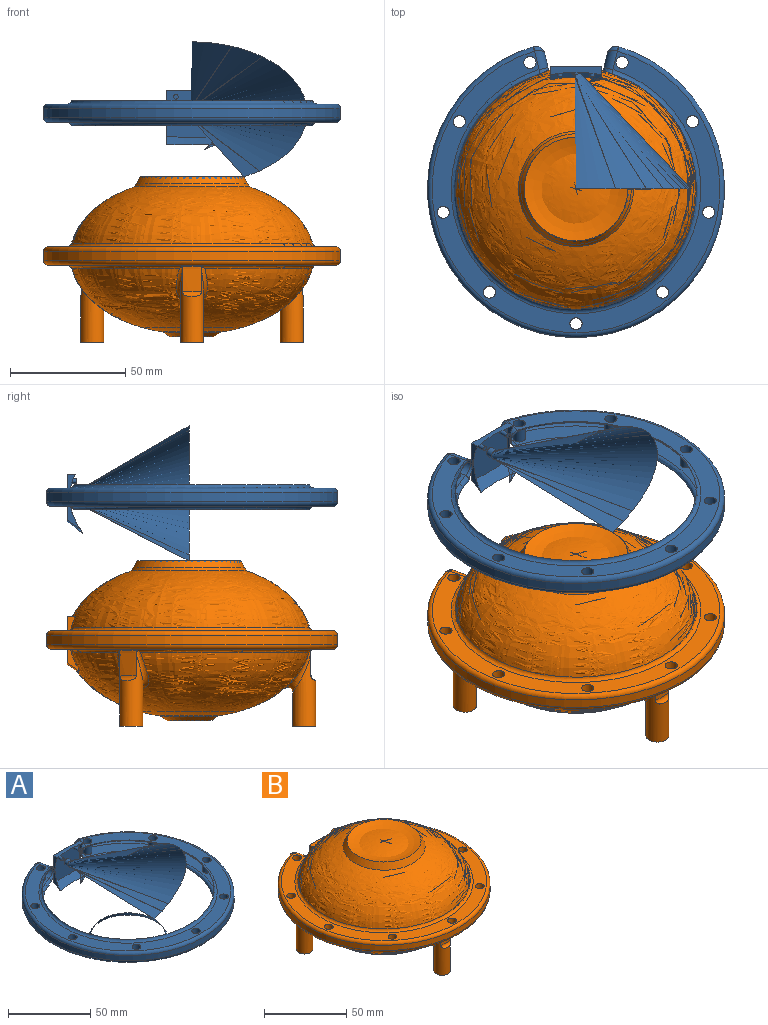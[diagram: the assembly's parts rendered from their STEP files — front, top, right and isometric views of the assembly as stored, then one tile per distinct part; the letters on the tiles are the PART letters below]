
ASSEMBLY  parts=2 mates=1
PART A: 52 faces, bbox 265.7x262.7x193.8 mm
  f0: plane 0.87x0.17mm, normal (0,0,-1), area 0.1mm2, adj f1,f50,f51
  f1: plane 22x20.66mm, normal (0,1,0), area 430mm2, adj f0,f2,f4,f5,f45,f46,f48,f50
  f2: cylinder r=2mm len=4mm, axis (0,-1,0), area 38.2mm2, adj f1,f3
  f3: revolved ~4x4mm, area 12.6mm2, adj f2
  f4: plane 0.87x0.17mm, normal (0,0,-1), area 0.1mm2, adj f1,f45,f50
  f5: plane 22x3.51mm, normal (0,0,1), area 59.5mm2, adj f1,f6,f45,f51
  f6: revolved ~105.61x105.6mm, area -70091.5mm2, adj f5,f7,f8,f37,f38,f39,f40,f41
  f7: plane 127.13x126.3mm, normal (0.97,-0.22,0), area 0.1mm2, adj f6,f8,f42
  f8: bspline ~6.62x5.74mm, area 9.9mm2, adj f6,f7,f9,f37
  f9: cylinder r=4mm len=8.95mm, axis (-0.22,-0.97,0), area 45.6mm2, adj f8,f10,f35,f36
  f10: cylinder r=4mm len=8.95mm, axis (0.22,0.97,0), area 45.6mm2, adj f9,f11,f34,f42
  f11: plane 125x122.37mm, normal (0,0,1), area 2542.7mm2, adj f10,f12,f22,f23,f24,f25,f26,f27
  f12: torus R=62.5mm, axis (0,0,1), area 1141.4mm2, adj f11,f13,f22,f24
  f13: cylinder r=64.5mm len=129mm, axis (0,0,1), area 1469.8mm2, adj f12,f14,f16,f21
  f14: cylinder r=4mm len=5.05mm, axis (0,0,1), area 17.1mm2, adj f13,f15,f22,f34,f35
  f15: torus R=2mm, axis (0,0,-1), area 0.7mm2, adj f14,f21,f35,f36
  f16: cylinder r=4mm len=5.05mm, axis (0,0,1), area 17.1mm2, adj f13,f17,f18,f20,f24
  f17: bspline ~5.54x4mm, area 8.7mm2, adj f16,f23,f24
  f18: bspline ~5.54x4mm, area 8.7mm2, adj f16,f19,f20
  f19: cylinder r=4mm len=8.95mm, axis (-0.22,0.97,0), area 45.6mm2, adj f18,f23,f36,f38
  f20: torus R=2mm, axis (0,0,-1), area 0.7mm2, adj f16,f18,f21,f36
  f21: torus R=62.5mm, axis (0,0,-1), area 1141.4mm2, adj f13,f15,f20,f36
  f22: torus R=2mm, axis (0,0,1), area 0.7mm2, adj f11,f12,f14,f34
  f23: cylinder r=4mm len=8.95mm, axis (0.22,-0.97,0), area 45.6mm2, adj f11,f17,f19,f40
  f24: torus R=2mm, axis (0,0,1), area 0.7mm2, adj f11,f12,f16,f17
  f25: cylinder r=2.65mm len=8mm, axis (0,0,1), area 133.2mm2, adj f11,f36
  f26: cylinder r=2.65mm len=8mm, axis (0,0,1), area 133.2mm2, adj f11,f36
  f27: cylinder r=2.65mm len=8mm, axis (0,0,1), area 133.2mm2, adj f11,f36
  f28: cylinder r=2.65mm len=8mm, axis (0,0,1), area 133.2mm2, adj f11,f36
  f29: cylinder r=2.65mm len=8mm, axis (0,0,1), area 133.2mm2, adj f11,f36
  f30: cylinder r=2.65mm len=8mm, axis (0,0,1), area 133.2mm2, adj f11,f36
  f31: cylinder r=2.65mm len=8mm, axis (0,0,1), area 133.2mm2, adj f11,f36
  f32: cylinder r=2.65mm len=8mm, axis (0,0,1), area 133.2mm2, adj f11,f36
  f33: cylinder r=2.65mm len=8mm, axis (0,0,1), area 133.2mm2, adj f11,f36
  f34: bspline ~5.54x4mm, area 8.7mm2, adj f10,f14,f22
  f35: bspline ~5.54x4mm, area 8.7mm2, adj f9,f14,f15
  f36: plane 125x122.37mm, normal (0,0,-1), area 2542.7mm2, adj f9,f15,f19,f20,f21,f25,f26,f27
  f37: torus R=54.25mm, axis (0,0,-1), area 798.1mm2, adj f6,f8,f36,f38
  f38: bspline ~6.62x5.74mm, area 9.9mm2, adj f6,f19,f37,f39
  f39: plane 127.13x126.3mm, normal (-0.97,-0.22,0), area 0.1mm2, adj f6,f38,f40
  f40: bspline ~6.62x5.74mm, area 9.9mm2, adj f6,f23,f39,f41
  f41: torus R=54.25mm, axis (0,0,-1), area 798.1mm2, adj f6,f11,f40,f42
  f42: bspline ~6.62x5.74mm, area 9.9mm2, adj f6,f7,f10,f41
  f43: cone r=22.5mm half-angle=29.3deg, axis (0,0,-1), area 447.5mm2, adj f6,f44
  f44: revolved ~22.5x22.5mm, area 0mm2, adj f43
  f45: plane 136.1x118.09mm, normal (-1,0,0), area 44.5mm2, adj f1,f4,f5,f6,f50
  f46: cylinder r=1mm len=4mm, axis (0,1,0), area 25.1mm2, adj f1,f47
  f47: plane 2x2mm, normal (0,1,0), area 3.1mm2, adj f46
  f48: cylinder r=1mm len=4mm, axis (0,1,0), area 25.1mm2, adj f1,f49
  f49: plane 2x2mm, normal (0,1,0), area 3.1mm2, adj f48
  f50: cone r=53.96mm half-angle=55.7deg, axis (0,0,1), area 128.5mm2, adj f0,f1,f4,f6,f45,f51
  f51: plane 129.26x111.26mm, normal (1,0,0), area 44.5mm2, adj f0,f1,f5,f6,f50
PART B: 84 faces, bbox 265.7x262.7x197.8 mm
  f0: revolved ~105.85x105.81mm, area -61415.2mm2, adj f4,f5,f6,f16,f17,f19,f21,f41
  f1: cylinder r=53mm len=11mm, axis (0,0,1), area 90.7mm2, adj f6,f35,f40,f55
  f2: cylinder r=53mm len=11mm, axis (0,0,1), area 90.7mm2, adj f5,f31,f39,f55
  f3: cylinder r=53mm len=11mm, axis (0,0,1), area 90.7mm2, adj f4,f26,f30,f55
  f4: bspline ~19.96x13.54mm, area 132mm2, adj f0,f3,f26,f55
  f5: bspline ~19.96x13.43mm, area 132mm2, adj f0,f2,f31,f55
  f6: bspline ~19.96x13.43mm, area 132mm2, adj f0,f1,f35,f55
  f7: revolved ~19x19mm, area 95.4mm2, adj f10,f44
  f8: revolved ~28x28mm, area 126.5mm2, adj f42,f43
  f9: plane 0.87x0.17mm, normal (0,0,-1), area 0.1mm2, adj f17,f20,f21
  f10: plane 15.5x15.5mm, normal (0,0,-1), area 45.6mm2, adj f7,f14
  f11: revolved ~99.99x99.97mm, area 11093.7mm2, adj f12,f15,f45
  f12: cylinder r=7.75mm len=15.5mm, axis (0,0,-1), area 98.1mm2, adj f11,f13
  f13: plane 15.5x15.5mm, normal (0,0,1), area 45.6mm2, adj f12,f14
  f14: cylinder r=6.75mm len=13.5mm, axis (0,0,-1), area 42.4mm2, adj f10,f13
  f15: cylinder r=2mm len=4mm, axis (0,-1,0), area 38.8mm2, adj f11,f20
  f16: plane 134.18x115.69mm, normal (0,0,1), area 59.5mm2, adj f0,f17,f19,f20
  f17: plane 129.32x111.32mm, normal (1,0,0), area 44.5mm2, adj f0,f9,f16,f20,f21
  f18: plane 0.87x0.17mm, normal (0,0,-1), area 0.1mm2, adj f19,f20,f21
  f19: plane 135.84x117.84mm, normal (-1,0,0), area 44.5mm2, adj f0,f16,f18,f20,f21
  f20: plane 22x20.66mm, normal (0,1,0), area 430mm2, adj f9,f15,f16,f17,f18,f19,f21,f22
  f21: cone r=53.96mm half-angle=55.7deg, axis (0,0,1), area 128.5mm2, adj f0,f9,f17,f18,f19,f20
  f22: cylinder r=1mm len=4mm, axis (0,1,0), area 25.1mm2, adj f20,f23
  f23: plane 2x2mm, normal (0,1,0), area 3.1mm2, adj f22
  f24: cylinder r=1mm len=4mm, axis (0,1,0), area 25.1mm2, adj f20,f25
  f25: plane 2x2mm, normal (0,1,0), area 3.1mm2, adj f24
  f26: cylinder r=5mm len=31.57mm, axis (0,0,1), area 640.7mm2, adj f3,f4,f28,f30
  f27: cylinder r=1.9mm len=30.49mm, axis (0,0,1), area 315.7mm2, adj f28,f29
  f28: plane 10x10mm, normal (0,0,-1), area 67.2mm2, adj f26,f27
  f29: revolved ~7.43x3.94mm, area 24.7mm2, adj f27
  f30: torus R=55mm, axis (0,0,-1), area 13mm2, adj f3,f26
  f31: cylinder r=5mm len=31.57mm, axis (0,0,1), area 640.7mm2, adj f2,f5,f33,f39
  f32: cylinder r=1.9mm len=30.49mm, axis (0,0,1), area 315.7mm2, adj f33,f34
  f33: plane 10x10mm, normal (0,0,-1), area 67.2mm2, adj f31,f32
  f34: revolved ~105.07x105.07mm, area 54809.1mm2, adj f32
  f35: cylinder r=5mm len=31.57mm, axis (0,0,1), area 640.7mm2, adj f1,f6,f37,f40
  f36: cylinder r=1.9mm len=30.49mm, axis (0,0,1), area 315.7mm2, adj f37,f38
  f37: plane 10x10mm, normal (0,0,-1), area 67.2mm2, adj f35,f36
  f38: revolved ~105.33x105.33mm, area 54809.1mm2, adj f36
  f39: torus R=55mm, axis (0,0,-1), area 13mm2, adj f2,f31
  f40: torus R=55mm, axis (0,0,-1), area 13mm2, adj f1,f35
  f41: plane 42.8x42.8mm, normal (0,0,-1), area 823mm2, adj f0,f42
  f42: cylinder r=14mm len=28mm, axis (0,0,-1), area 146.8mm2, adj f8,f41
  f43: cone r=9.5mm half-angle=55.2deg, axis (0,0,1), area 252.6mm2, adj f8,f44
  f44: cylinder r=9.5mm len=19mm, axis (0,0,1), area 100.5mm2, adj f7,f43
  f45: cylinder r=8mm len=16mm, axis (0,0,1), area 40.1mm2, adj f11,f47
  f46: cone r=22.5mm half-angle=30.2deg, axis (0,0,-1), area 741.3mm2, adj f0,f47
  f47: revolved ~45x45mm, area 1424.2mm2, adj f45,f46
  f48: plane 125x122.37mm, normal (0,0,-1), area 2542.7mm2, adj f53,f55,f61,f64,f67,f73,f75,f76
  f49: cylinder r=64.5mm len=129mm, axis (0,0,1), area 1469.8mm2, adj f53,f54,f60,f68
  f50: plane 125x122.37mm, normal (0,0,1), area 2542.7mm2, adj f54,f56,f57,f62,f66,f72,f75,f76
  f51: plane 10.81x9.98mm, normal (0.97,0.22,0), area 0.1mm2, adj f0,f58,f65
  f52: plane 127.13x126.3mm, normal (-0.97,0.22,0), area 0.1mm2, adj f0,f70,f74
  f53: torus R=62.5mm, axis (0,0,1), area 1141.4mm2, adj f48,f49,f61,f67
  f54: torus R=62.5mm, axis (0,0,-1), area 1141.4mm2, adj f49,f50,f57,f66
  f55: torus R=54.25mm, axis (0,0,-1), area 760.1mm2, adj f0,f1,f2,f3,f4,f5,f6,f48
  f56: torus R=54.25mm, axis (0,0,-1), area 798.1mm2, adj f0,f50,f58,f70
  f57: torus R=2mm, axis (0,0,-1), area 0.7mm2, adj f50,f54,f59,f60
  f58: bspline ~6.62x5.74mm, area 12.3mm2, adj f0,f51,f56,f62
  f59: bspline ~5.54x4mm, area 8.7mm2, adj f57,f60,f62
  f60: cylinder r=4mm len=5.05mm, axis (0,0,1), area 17.1mm2, adj f49,f57,f59,f61,f63
  f61: torus R=2mm, axis (0,0,1), area 0.7mm2, adj f48,f53,f60,f63
  f62: cylinder r=4mm len=8.95mm, axis (-0.22,0.97,0), area 45.6mm2, adj f50,f58,f59,f64
  f63: bspline ~5.54x4mm, area 8.7mm2, adj f60,f61,f64
  f64: cylinder r=4mm len=8.95mm, axis (0.22,-0.97,0), area 45.6mm2, adj f48,f62,f63,f65
  f65: bspline ~6.62x5.74mm, area 9.9mm2, adj f0,f51,f55,f64
  f66: torus R=2mm, axis (0,0,-1), area 0.7mm2, adj f50,f54,f68,f69
  f67: torus R=2mm, axis (0,0,1), area 0.7mm2, adj f48,f53,f68,f71
  f68: cylinder r=4mm len=5.05mm, axis (0,0,1), area 17.1mm2, adj f49,f66,f67,f69,f71
  f69: bspline ~5.54x4mm, area 8.7mm2, adj f66,f68,f72
  f70: bspline ~6.62x5.74mm, area 9.9mm2, adj f0,f52,f56,f72
  f71: bspline ~5.54x4mm, area 8.7mm2, adj f67,f68,f73
  f72: cylinder r=4mm len=8.95mm, axis (-0.22,-0.97,0), area 45.6mm2, adj f50,f69,f70,f73
  f73: cylinder r=4mm len=8.95mm, axis (0.22,0.97,0), area 45.6mm2, adj f48,f71,f72,f74
  f74: bspline ~6.62x5.74mm, area 9.9mm2, adj f0,f52,f55,f73
  f75: cylinder r=2.65mm len=8mm, axis (0,0,1), area 133.2mm2, adj f48,f50
  f76: cylinder r=2.65mm len=8mm, axis (0,0,1), area 133.2mm2, adj f48,f50
  f77: cylinder r=2.65mm len=8mm, axis (0,0,1), area 133.2mm2, adj f48,f50
  f78: cylinder r=2.65mm len=8mm, axis (0,0,1), area 133.2mm2, adj f48,f50
  f79: cylinder r=2.65mm len=8mm, axis (0,0,1), area 133.2mm2, adj f48,f50
  f80: cylinder r=2.65mm len=8mm, axis (0,0,1), area 133.2mm2, adj f48,f50
  f81: cylinder r=2.65mm len=8mm, axis (0,0,1), area 133.2mm2, adj f48,f50
  f82: cylinder r=2.65mm len=8mm, axis (0,0,1), area 133.2mm2, adj f48,f50
  f83: cylinder r=2.65mm len=8mm, axis (0,0,1), area 133.2mm2, adj f48,f50
PLACE A t=(-42.06,-26.18,38.88)mm
PLACE B t=(-42.06,-26.18,-23.12)mm fixed
MATE slider B.f1 <-> A.f12  axis (0,0,-1) through (-42.06,-26.18,42.19)mm
